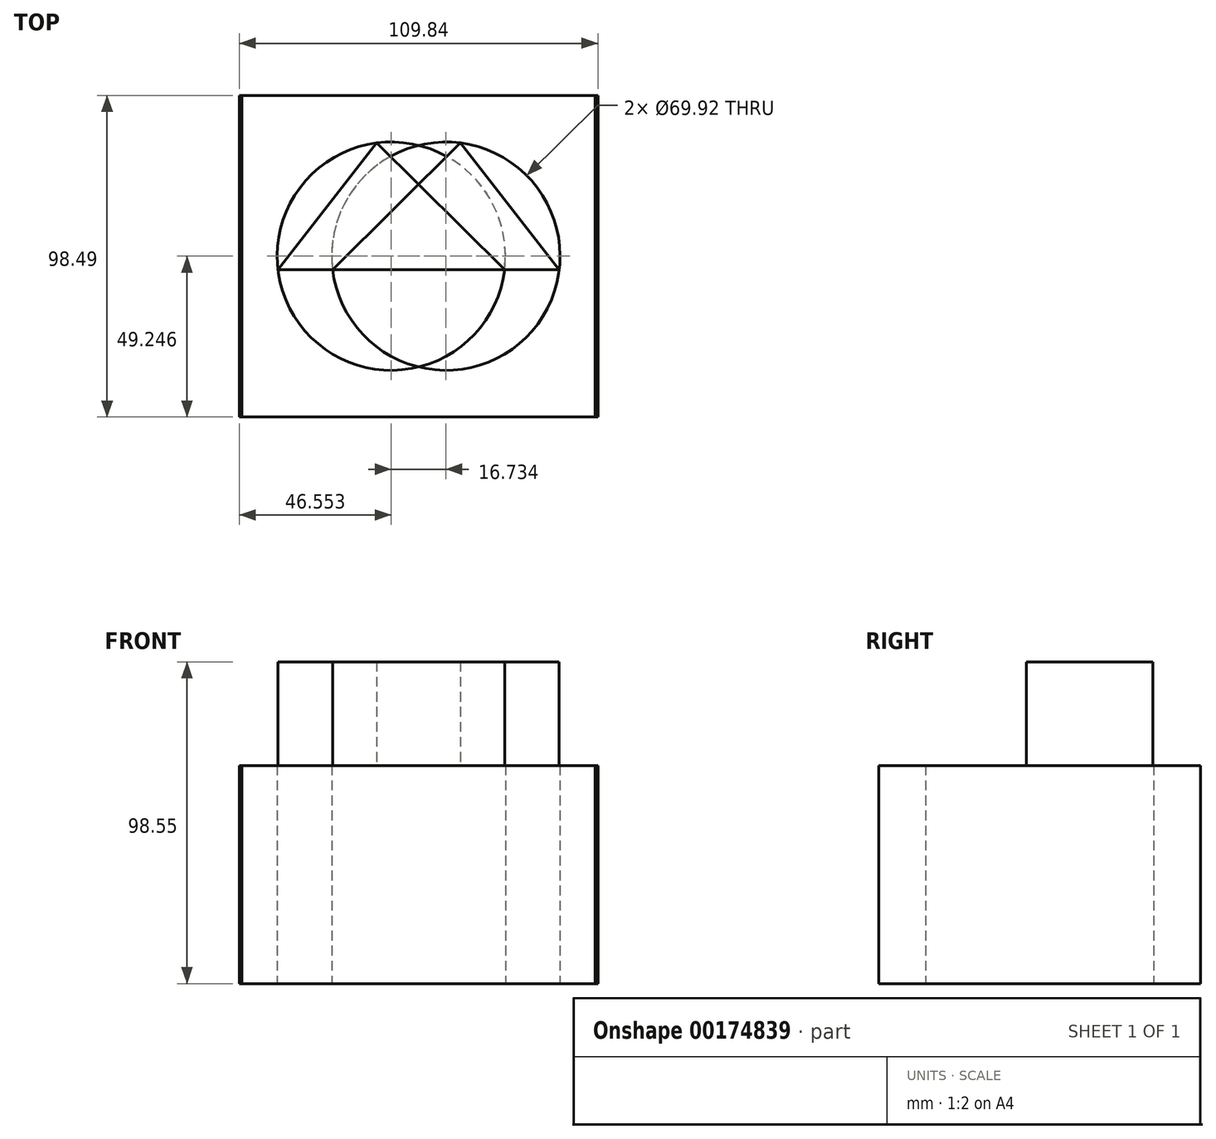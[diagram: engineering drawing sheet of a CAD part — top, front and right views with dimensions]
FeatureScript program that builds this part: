
annotation { "Feature Type Name" : "Feature", "Feature Type Description" : "" }
export const myFeature = defineFeature(function(context is Context, id is Id, definition is map)
    precondition{}
    {
        {
            var Q0;
            Q0=qCreatedBy(makeId("Top.planeOp"),FACE);
            var sketch = newSketch(context, id + "F0", { "sketchPlane" : qUnion([Q0])});
            skLineSegment(sketch, "E0.bottom", {"start": v(-54.92, 44.04) * mm, "end": v(54.1, 44.04) * mm});
            skLineSegment(sketch, "E0.top", {"start": v(-54.92, -54.45) * mm, "end": v(54.1, -54.45) * mm});
            skLineSegment(sketch, "E0.left", {"start": v(-54.92, 44.04) * mm, "end": v(-54.92, -54.45) * mm});
            skLineSegment(sketch, "E0.right", {"start": v(54.1, 44.04) * mm, "end": v(54.1, -54.45) * mm});
            skCircle(sketch, "E1", {"center": v(-8.37, -5.2) * mm, "radius": 34.96 * mm});
            skPoint(sketch, "E1.centerSnap0", {"position": v(-54.92, -5.2) * mm});
            skSolve(sketch);
        }
        {
            var Q0;
            Q0=makeQuery(id+"F0.imprint","IMPRINT",FACE,{"disambiguationData":[TD([[makeQuery(id+"F0.imprint","IMPRINT",EDGE,{"derivedFrom":sQuery(id+"F0.wireOp",EDGE,"E0.bottom")}),-1.0]])]});
            extrude(context, id + "F1", {"entities" : qUnion([Q0]), "depth" : 66.8 * mm});
        }
        {
            var Q0;
            Q0=makeQuery(id+"F1.opExtrude","CAP_FACE",FACE,{"disambiguationData":[OSD([sQuery(id+"F0.wireOp",EDGE,"E0.bottom"),sQuery(id+"F0.wireOp",EDGE,"E0.top"),sQuery(id+"F0.wireOp",EDGE,"E0.left"),sQuery(id+"F0.wireOp",EDGE,"E0.right"),sQuery(id+"F0.wireOp",EDGE,"E1")])],"isStart":false});
            var sketch = newSketch(context, id + "F2", { "sketchPlane" : qUnion([Q0])});
            skLineSegment(sketch, "E2", {"start": v(-43.08, -9.32) * mm, "end": v(-43.08, 66.14) * mm});
            skLineSegment(sketch, "E3", {"start": v(-43.08, 66.14) * mm, "end": v(26.35, -9.32) * mm});
            skLineSegment(sketch, "E4", {"start": v(26.35, -9.32) * mm, "end": v(-43.08, -9.32) * mm});
            skLineSegment(sketch, "E5", {"start": v(-43.08, 66.14) * mm, "end": v(-12.83, 29.47) * mm});
            skLineSegment(sketch, "E6", {"start": v(-43.08, -9.32) * mm, "end": v(-12.83, 29.47) * mm});
            skLineSegment(sketch, "E7", {"start": v(-12.83, 29.47) * mm, "end": v(26.35, -9.32) * mm});
            skSolve(sketch);
        }
        {
            var Q0;
            Q0=makeQuery(id+"F2.imprint","IMPRINT",FACE,{"disambiguationData":[TD([[makeQuery(id+"F2.imprint","IMPRINT",EDGE,{"derivedFrom":sQuery(id+"F2.wireOp",EDGE,"E4")}),-1.0]])]});
            extrude(context, id + "F3", {"entities" : qUnion([Q0]), "depth" : 31.75 * mm});
        }
        {
            var Q0;
            Q0=makeQuery(id+"F3.opExtrude","SWEPT_BODY",BODY,{"disambiguationData":[OSD([sQuery(id+"F2.wireOp",EDGE,"E4"),sQuery(id+"F2.wireOp",EDGE,"E6"),sQuery(id+"F2.wireOp",EDGE,"E7")])]});
            var Q1;
            Q1=makeQuery(id+"F1.opExtrude","SWEPT_BODY",BODY,{"disambiguationData":[OSD([sQuery(id+"F0.wireOp",EDGE,"E0.bottom"),sQuery(id+"F0.wireOp",EDGE,"E0.top"),sQuery(id+"F0.wireOp",EDGE,"E0.left"),sQuery(id+"F0.wireOp",EDGE,"E0.right"),sQuery(id+"F0.wireOp",EDGE,"E1")])]});
            var Q2;
            Q2=qCreatedBy(makeId("Right.planeOp"),FACE);
            mirror(context, id + "F4", {"entities" : qUnion([Q0, Q1]), "mirrorPlane" : qUnion([Q2])});
        }
    });
